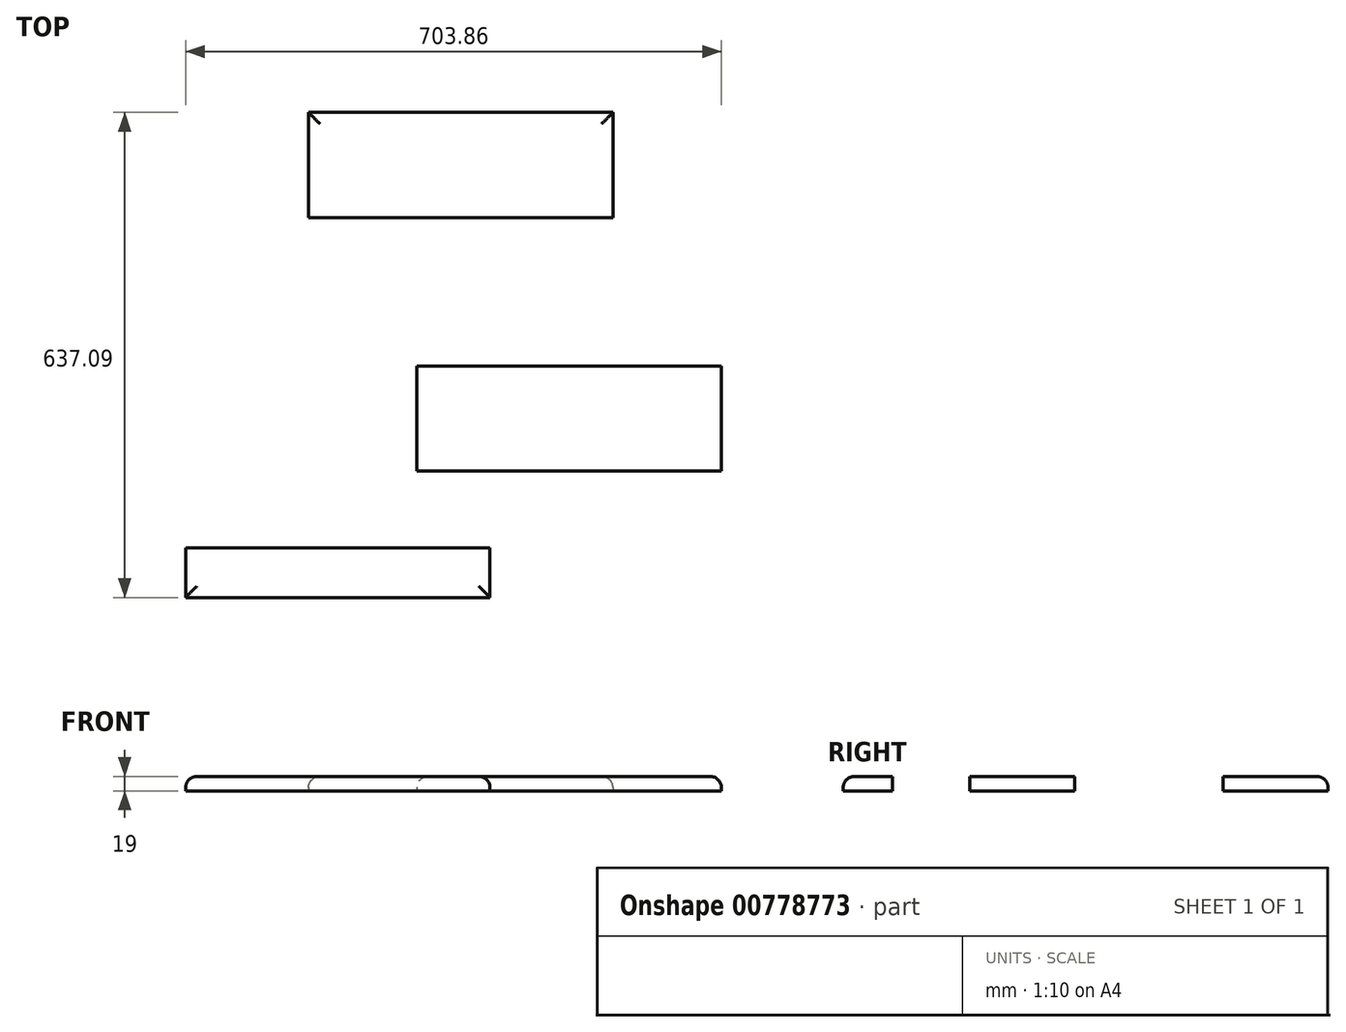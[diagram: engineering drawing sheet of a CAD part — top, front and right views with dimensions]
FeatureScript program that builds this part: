
annotation { "Feature Type Name" : "Feature", "Feature Type Description" : "" }
export const myFeature = defineFeature(function(context is Context, id is Id, definition is map)
    precondition{}
    {
        {
            var Q0;
            Q0=qCreatedBy(makeId("Top.planeOp"),FACE);
            var sketch = newSketch(context, id + "F0", { "sketchPlane" : qUnion([Q0])});
            skLineSegment(sketch, "E0.bottom", {"start": v(-221.08, -21.18) * mm, "end": v(178.92, -21.18) * mm});
            skLineSegment(sketch, "E0.top", {"start": v(-221.08, -159.18) * mm, "end": v(178.92, -159.18) * mm});
            skLineSegment(sketch, "E0.left", {"start": v(-221.08, -21.18) * mm, "end": v(-221.08, -159.18) * mm});
            skLineSegment(sketch, "E0.right", {"start": v(178.92, -21.18) * mm, "end": v(178.92, -159.18) * mm});
            skLineSegment(sketch, "E1.bottom", {"start": v(-363.4, 311.76) * mm, "end": v(36.6, 311.76) * mm});
            skLineSegment(sketch, "E1.top", {"start": v(-363.4, 173.76) * mm, "end": v(36.6, 173.76) * mm});
            skLineSegment(sketch, "E1.left", {"start": v(-363.4, 311.76) * mm, "end": v(-363.4, 173.76) * mm});
            skLineSegment(sketch, "E1.right", {"start": v(36.6, 311.76) * mm, "end": v(36.6, 173.76) * mm});
            skLineSegment(sketch, "E2.bottom", {"start": v(-524.94, -325.33) * mm, "end": v(-124.94, -325.33) * mm});
            skLineSegment(sketch, "E2.top", {"start": v(-524.94, -260.33) * mm, "end": v(-124.94, -260.33) * mm});
            skLineSegment(sketch, "E2.left", {"start": v(-524.94, -325.33) * mm, "end": v(-524.94, -260.33) * mm});
            skLineSegment(sketch, "E2.right", {"start": v(-124.94, -325.33) * mm, "end": v(-124.94, -260.33) * mm});
            skSolve(sketch);
        }
        {
            var Q0;
            Q0 = qSketchRegion(id + "F0", true);
            extrude(context, id + "F1", {"entities" : qUnion([Q0]), "depth" : 19 * mm, "offsetDistance" : 25 * mm});
        }
        {
            var Q0;
            Q0=makeQuery(id+"F1.opExtrude","CAP_EDGE",EDGE,{"disambiguationData":[OSD([sQuery(id+"F0.wireOp",EDGE,"E2.bottom")])],"isStart":false});
            var Q1;
            Q1=makeQuery(id+"F1.opExtrude","CAP_EDGE",EDGE,{"disambiguationData":[OSD([sQuery(id+"F0.wireOp",EDGE,"E2.right")])],"isStart":false});
            var Q2;
            Q2=makeQuery(id+"F1.opExtrude","CAP_EDGE",EDGE,{"disambiguationData":[OSD([sQuery(id+"F0.wireOp",EDGE,"E2.left")])],"isStart":false});
            var Q3;
            Q3=makeQuery(id+"F1.opExtrude","CAP_EDGE",EDGE,{"disambiguationData":[OSD([sQuery(id+"F0.wireOp",EDGE,"E0.left")])],"isStart":false});
            var Q4;
            Q4=makeQuery(id+"F1.opExtrude","CAP_EDGE",EDGE,{"disambiguationData":[OSD([sQuery(id+"F0.wireOp",EDGE,"E0.right")])],"isStart":false});
            var Q5;
            Q5=makeQuery(id+"F1.opExtrude","CAP_EDGE",EDGE,{"disambiguationData":[OSD([sQuery(id+"F0.wireOp",EDGE,"E1.right")])],"isStart":false});
            var Q6;
            Q6=makeQuery(id+"F1.opExtrude","CAP_EDGE",EDGE,{"disambiguationData":[OSD([sQuery(id+"F0.wireOp",EDGE,"E1.bottom")])],"isStart":false});
            var Q7;
            Q7=makeQuery(id+"F1.opExtrude","CAP_EDGE",EDGE,{"disambiguationData":[OSD([sQuery(id+"F0.wireOp",EDGE,"E1.left")])],"isStart":false});
            fillet(context, id + "F2", {"entities" : qUnion([Q0, Q1, Q2, Q3, Q4, Q5, Q6, Q7]), "radius" : 15 * mm, "tangentPropagation" : true, "allowEdgeOverflow" : false});
        }
    });
